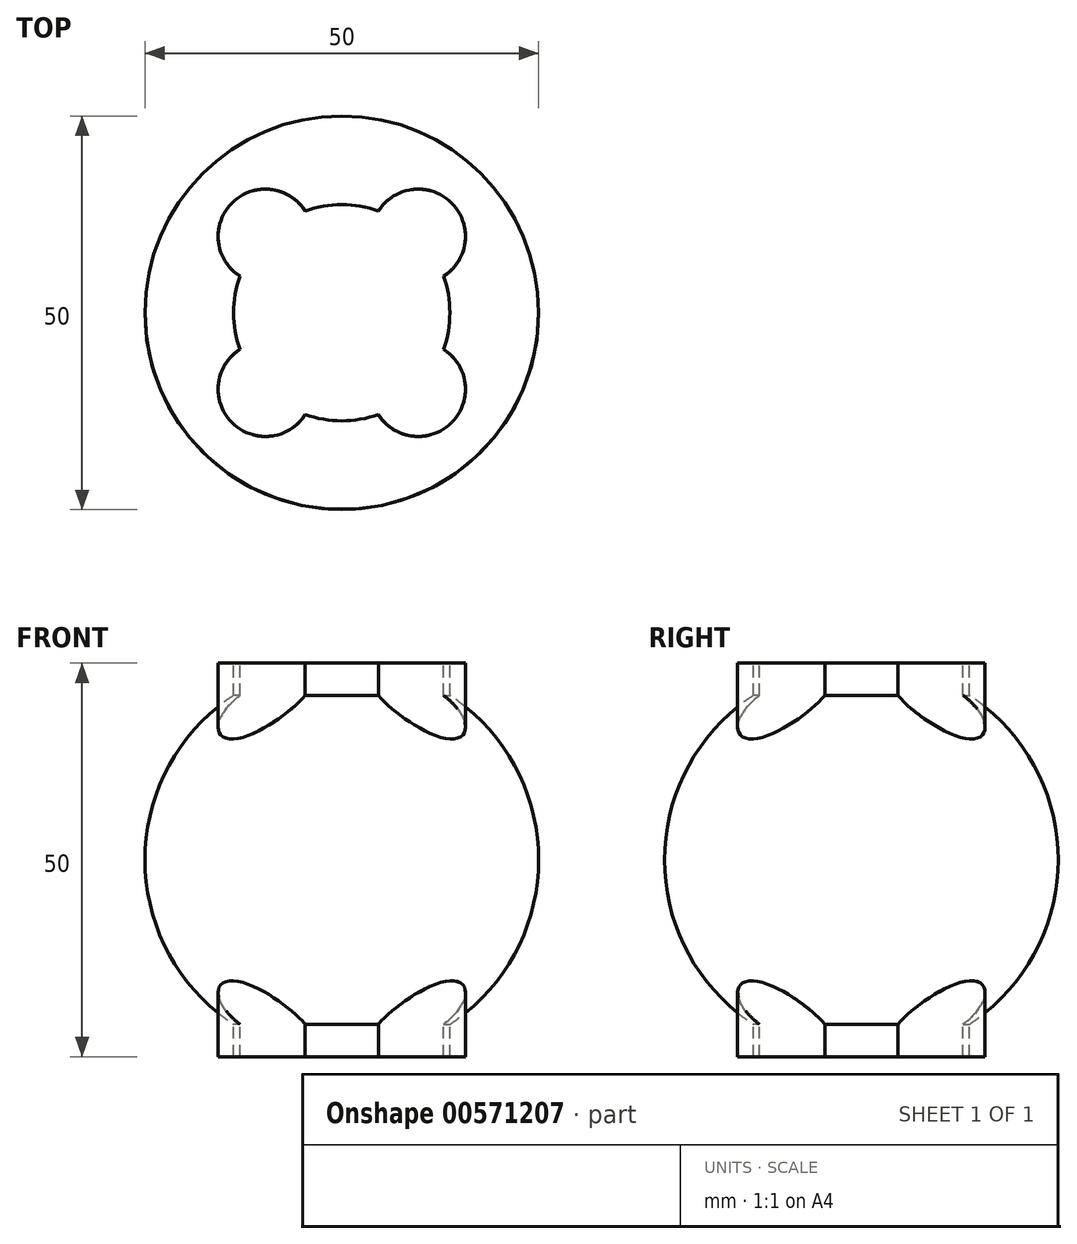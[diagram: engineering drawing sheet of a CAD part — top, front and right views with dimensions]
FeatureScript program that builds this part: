
annotation { "Feature Type Name" : "Feature", "Feature Type Description" : "" }
export const myFeature = defineFeature(function(context is Context, id is Id, definition is map)
    precondition{}
    {
        {
            var Q0;
            Q0=qCreatedBy(makeId("Front.planeOp"),FACE);
            var sketch = newSketch(context, id + "F0", { "sketchPlane" : qUnion([Q0])});
            skCircle(sketch, "E0", {"center": v(0, 0) * mm, "radius": 25 * mm});
            skLineSegment(sketch, "E1", {"start": v(-50.72, 0) * mm, "end": v(49.3, 0) * mm});
            skSolve(sketch);
        }
        {
            var Q0;
            {var subQ0=sQuery(id+"F0.wireOp",EDGE,"E1");var subQ1=sQuery(id+"F0.wireOp",EDGE,"E0");var subQ2=makeQuery(id+"F0.imprint","INTERSECT",VERTEX,{"disambiguationData":[OD(0.0)],"derivedFrom":[subQ1,subQ0]});Q0=makeQuery(id+"F0.imprint","IMPRINT",FACE,{"disambiguationData":[TD([[makeQuery(id+"F0.imprint","IMPRINT",EDGE,{"disambiguationData":[TD([[subQ2,-1.0]])],"derivedFrom":subQ1}),1.0]])]});}
            var Q1;
            Q1=sQuery(id+"F0.wireOp",EDGE,"E1");
            revolve(context, id + "F1", {"entities" : qUnion([Q0]), "axis" : qUnion([Q1]), "revolveType" : RevolveType.FULL});
        }
        {
            var Q0;
            Q0=qCreatedBy(makeId("Top.planeOp"),FACE);
            cPlane(context, id + "F2", {"entities" : qUnion([Q0]), "cplaneType" : CPlaneType.OFFSET, "offset" : 25 * mm, "width" : 150 * mm, "height" : 150 * mm});
        }
        {
            var Q0;
            Q0=qCreatedBy(id+"F2.planeOp",FACE);
            var sketch = newSketch(context, id + "F3", { "sketchPlane" : qUnion([Q0])});
            skCircle(sketch, "E2", {"center": v(-9.7, 9.7) * mm, "radius": 6 * mm});
            skArc(sketch, "E3", {"start": v(-12.92, 4.64) * mm, "mid": v(-13.73, 0) * mm, "end": v(-12.92, -4.64) * mm});
            skLineSegment(sketch, "E4", {"start": v(0, 0) * mm, "end": v(-9.7, 9.7) * mm});
            skLineSegment(sketch, "E5", {"start": v(0, 0) * mm, "end": v(9.7, 9.7) * mm});
            skCircle(sketch, "E6", {"center": v(9.7, 9.7) * mm, "radius": 6 * mm});
            skLineSegment(sketch, "E7", {"start": v(0, 0) * mm, "end": v(9.7, -9.7) * mm});
            skLineSegment(sketch, "E8", {"start": v(9.7, -9.7) * mm, "end": v(0, 0) * mm});
            skLineSegment(sketch, "E9", {"start": v(0, 0) * mm, "end": v(-9.7, -9.7) * mm});
            skCircle(sketch, "E10", {"center": v(-9.7, -9.7) * mm, "radius": 6 * mm});
            skCircle(sketch, "E11", {"center": v(9.7, -9.7) * mm, "radius": 6 * mm});
            skArc(sketch, "E12.trimOffspring", {"start": v(-4.64, -12.92) * mm, "mid": v(0, -13.73) * mm, "end": v(4.64, -12.92) * mm});
            skArc(sketch, "E13.trimOffspring", {"start": v(12.92, -4.64) * mm, "mid": v(13.73, 0) * mm, "end": v(12.92, 4.64) * mm});
            skArc(sketch, "E14.trimOffspring", {"start": v(4.64, 12.92) * mm, "mid": v(0, 13.73) * mm, "end": v(-4.64, 12.92) * mm});
            skSolve(sketch);
        }
        {
            var Q0;
            Q0 = qSketchRegion(id + "F3", true);
            extrude(context, id + "F4", {"entities" : qUnion([Q0]), "operationType" : NewBodyOperationType.REMOVE, "oppositeDirection" : true, "depth" : 50 * mm, "offsetDistance" : 25 * mm});
        }
        {
            var Q0;
            Q0 = qSketchRegion(id + "F3", true);
            extrude(context, id + "F5", {"entities" : qUnion([Q0]), "operationType" : NewBodyOperationType.ADD, "oppositeDirection" : true, "depth" : 50 * mm, "offsetDistance" : 25 * mm});
        }
    });
